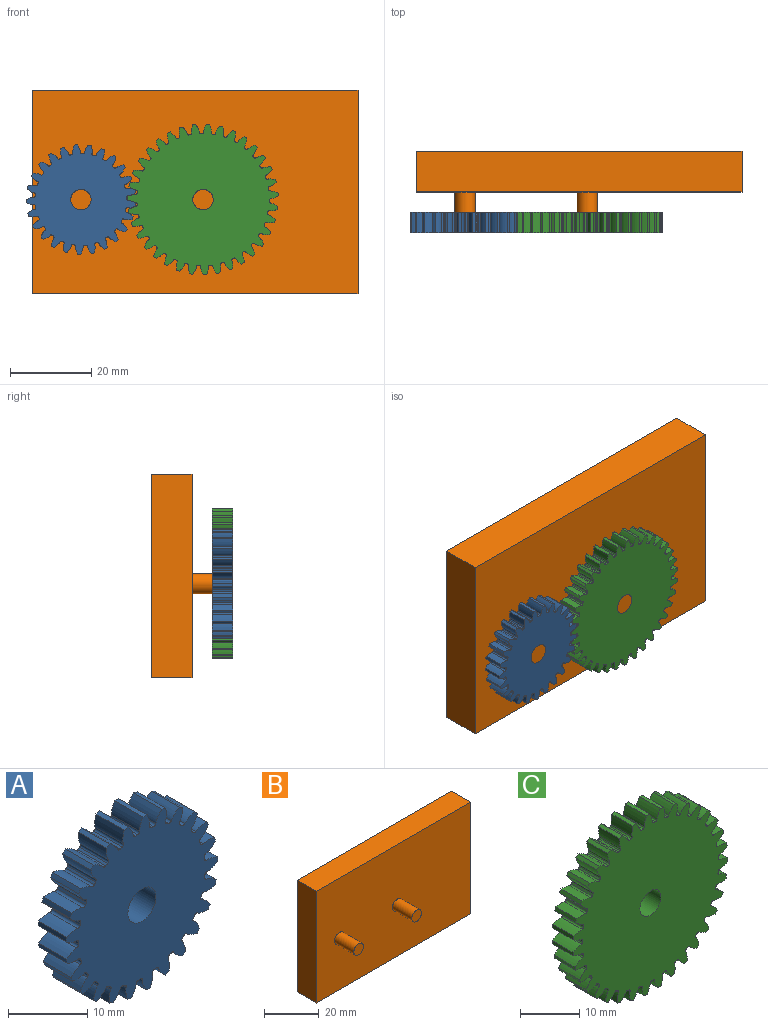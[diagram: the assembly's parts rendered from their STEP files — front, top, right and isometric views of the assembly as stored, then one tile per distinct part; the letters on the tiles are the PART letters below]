
ASSEMBLY  parts=3 mates=2
PART A: 153 faces, bbox 27x5x27 mm
  f0: extruded ~5x1.94mm, area 10.1mm2, adj f100,f101,f102,f103
  f1: cylinder r=11.25mm len=5mm, axis (0,1,0), area 1.9mm2, adj f101,f102,f103,f104
  f2: extruded ~5x1.71mm, area 10.1mm2, adj f3,f101,f102,f104
  f3: cylinder r=13.5mm len=5mm, axis (0,1,0), area 3.6mm2, adj f2,f4,f101,f102
  f4: extruded ~5x2mm, area 10.1mm2, adj f3,f101,f102,f105
  f5: cylinder r=11.25mm len=5mm, axis (0,1,0), area 1.9mm2, adj f101,f102,f105,f106
  f6: extruded ~5x1.44mm, area 10.1mm2, adj f7,f101,f102,f106
  f7: cylinder r=13.5mm len=5mm, axis (0,1,0), area 3.6mm2, adj f6,f8,f101,f102
  f8: extruded ~5x1.94mm, area 10.1mm2, adj f7,f101,f102,f107
  f9: cylinder r=11.25mm len=5mm, axis (0,1,0), area 1.9mm2, adj f101,f102,f107,f108
  f10: extruded ~5x1.74mm, area 10.1mm2, adj f11,f101,f102,f108
  f11: cylinder r=13.5mm len=5mm, axis (0,1,0), area 3.6mm2, adj f10,f12,f101,f102
  f12: extruded ~5x1.76mm, area 10.1mm2, adj f11,f101,f102,f109
  f13: cylinder r=11.25mm len=5mm, axis (0,1,0), area 1.9mm2, adj f101,f102,f109,f110
  f14: extruded ~5x1.93mm, area 10.1mm2, adj f15,f101,f102,f110
  f15: cylinder r=13.5mm len=5mm, axis (0,1,0), area 3.6mm2, adj f14,f16,f101,f102
  f16: extruded ~5x1.46mm, area 10.1mm2, adj f15,f101,f102,f111
  f17: cylinder r=11.25mm len=5mm, axis (0,1,0), area 1.9mm2, adj f101,f102,f111,f112
  f18: extruded ~5x2mm, area 10.1mm2, adj f19,f101,f102,f112
  f19: cylinder r=13.5mm len=5mm, axis (0,1,0), area 3.6mm2, adj f18,f20,f101,f102
  f20: extruded ~5x1.69mm, area 10.1mm2, adj f19,f101,f102,f113
  f21: cylinder r=11.25mm len=5mm, axis (0,1,0), area 1.9mm2, adj f101,f102,f113,f114
  f22: extruded ~5x1.95mm, area 10.1mm2, adj f23,f101,f102,f114
  f23: cylinder r=13.5mm len=5mm, axis (0,1,0), area 3.6mm2, adj f22,f24,f101,f102
  f24: extruded ~5x1.9mm, area 10.1mm2, adj f23,f101,f102,f115
  f25: cylinder r=11.25mm len=5mm, axis (0,1,0), area 1.9mm2, adj f101,f102,f115,f116
  f26: extruded ~5x1.77mm, area 10.1mm2, adj f27,f101,f102,f116
  f27: cylinder r=13.5mm len=5mm, axis (0,1,0), area 3.6mm2, adj f26,f28,f101,f102
  f28: extruded ~5x2mm, area 10.1mm2, adj f27,f101,f102,f117
  f29: cylinder r=11.25mm len=5mm, axis (0,1,0), area 1.9mm2, adj f101,f102,f117,f118
  f30: extruded ~5x1.48mm, area 10.1mm2, adj f31,f101,f102,f118
  f31: cylinder r=13.5mm len=5mm, axis (0,1,0), area 3.6mm2, adj f30,f32,f101,f102
  f32: extruded ~5x1.97mm, area 10.1mm2, adj f31,f101,f102,f119
  f33: cylinder r=11.25mm len=5mm, axis (0,1,0), area 1.9mm2, adj f101,f102,f119,f120
  f34: extruded ~5x1.67mm, area 10.1mm2, adj f35,f101,f102,f120
  f35: cylinder r=13.5mm len=5mm, axis (0,1,0), area 3.6mm2, adj f34,f36,f101,f102
  f36: extruded ~5x1.81mm, area 10.1mm2, adj f35,f101,f102,f121
  f37: cylinder r=11.25mm len=5mm, axis (0,1,0), area 1.9mm2, adj f101,f102,f121,f122
  f38: extruded ~5x1.89mm, area 10.1mm2, adj f39,f101,f102,f122
  f39: cylinder r=13.5mm len=5mm, axis (0,1,0), area 3.6mm2, adj f38,f40,f101,f102
  f40: extruded ~5x1.54mm, area 10.1mm2, adj f39,f101,f102,f123
  f41: cylinder r=11.25mm len=5mm, axis (0,1,0), area 1.9mm2, adj f101,f102,f123,f124
  f42: extruded ~5x2mm, area 10.1mm2, adj f43,f101,f102,f124
  f43: cylinder r=13.5mm len=5mm, axis (0,1,0), area 3.6mm2, adj f42,f44,f101,f102
  f44: extruded ~5x1.62mm, area 10.1mm2, adj f43,f101,f102,f125
  f45: cylinder r=11.25mm len=5mm, axis (0,1,0), area 1.9mm2, adj f101,f102,f125,f126
  f46: extruded ~5x1.97mm, area 10.1mm2, adj f47,f101,f102,f126
  f47: cylinder r=13.5mm len=5mm, axis (0,1,0), area 3.6mm2, adj f46,f48,f101,f102
  f48: extruded ~5x1.86mm, area 10.1mm2, adj f47,f101,f102,f127
  f49: cylinder r=11.25mm len=5mm, axis (0,1,0), area 1.9mm2, adj f101,f102,f127,f128
  f50: extruded ~5x1.83mm, area 10.1mm2, adj f51,f101,f102,f128
  f51: cylinder r=13.5mm len=5mm, axis (0,1,0), area 3.6mm2, adj f50,f52,f101,f102
  f52: extruded ~5x1.99mm, area 10.1mm2, adj f51,f101,f102,f129
  f53: cylinder r=11.25mm len=5mm, axis (0,1,0), area 1.9mm2, adj f101,f102,f129,f130
  f54: extruded ~5x1.56mm, area 10.1mm2, adj f55,f101,f102,f130
  f55: cylinder r=13.5mm len=5mm, axis (0,1,0), area 3.6mm2, adj f54,f56,f101,f102
  f56: extruded ~5x1.99mm, area 10.1mm2, adj f55,f101,f102,f131
  f57: cylinder r=11.25mm len=5mm, axis (0,1,0), area 1.9mm2, adj f101,f102,f131,f132
  f58: extruded ~5x1.6mm, area 10.1mm2, adj f59,f101,f102,f132
  f59: cylinder r=13.5mm len=5mm, axis (0,1,0), area 3.6mm2, adj f58,f60,f101,f102
  f60: extruded ~5x1.86mm, area 10.1mm2, adj f59,f101,f102,f133
  f61: cylinder r=11.25mm len=5mm, axis (0,1,0), area 1.9mm2, adj f101,f102,f133,f134
  f62: extruded ~5x1.85mm, area 10.1mm2, adj f63,f101,f102,f134
  f63: cylinder r=13.5mm len=5mm, axis (0,1,0), area 3.6mm2, adj f62,f64,f101,f102
  f64: extruded ~5x1.62mm, area 10.1mm2, adj f63,f101,f102,f135
  f65: cylinder r=11.25mm len=5mm, axis (0,1,0), area 1.9mm2, adj f101,f102,f135,f136
  f66: extruded ~5x1.98mm, area 10.1mm2, adj f67,f101,f102,f136
  f67: cylinder r=13.5mm len=5mm, axis (0,1,0), area 3.6mm2, adj f66,f68,f101,f102
  f68: extruded ~5x1.54mm, area 10.1mm2, adj f67,f101,f102,f137
  f69: cylinder r=11.25mm len=5mm, axis (0,1,0), area 1.9mm2, adj f101,f102,f137,f138
  f70: extruded ~5x1.99mm, area 10.1mm2, adj f71,f101,f102,f138
  f71: cylinder r=13.5mm len=5mm, axis (0,1,0), area 3.6mm2, adj f70,f72,f101,f102
  f72: extruded ~5x1.81mm, area 10.1mm2, adj f71,f101,f102,f139
  f73: cylinder r=11.25mm len=5mm, axis (0,1,0), area 1.9mm2, adj f101,f102,f139,f140
  f74: extruded ~5x1.87mm, area 10.1mm2, adj f75,f101,f102,f140
  f75: cylinder r=13.5mm len=5mm, axis (0,1,0), area 3.6mm2, adj f74,f76,f101,f102
  f76: extruded ~5x1.97mm, area 10.1mm2, adj f75,f101,f102,f141
  f77: cylinder r=11.25mm len=5mm, axis (0,1,0), area 1.9mm2, adj f101,f102,f141,f142
  f78: extruded ~5x1.64mm, area 10.1mm2, adj f79,f101,f102,f142
  f79: cylinder r=13.5mm len=5mm, axis (0,1,0), area 3.6mm2, adj f78,f80,f101,f102
  f80: extruded ~5x2mm, area 10.1mm2, adj f79,f101,f102,f143
  f81: cylinder r=11.25mm len=5mm, axis (0,1,0), area 1.9mm2, adj f101,f102,f143,f144
  f82: extruded ~5x1.52mm, area 10.1mm2, adj f83,f101,f102,f144
  f83: cylinder r=13.5mm len=5mm, axis (0,1,0), area 3.6mm2, adj f82,f84,f101,f102
  f84: extruded ~5x1.9mm, area 10.1mm2, adj f83,f101,f102,f145
  f85: cylinder r=11.25mm len=5mm, axis (0,1,0), area 1.9mm2, adj f101,f102,f145,f146
  f86: extruded ~5x1.8mm, area 10.1mm2, adj f87,f101,f102,f146
  f87: cylinder r=13.5mm len=5mm, axis (0,1,0), area 3.6mm2, adj f86,f88,f101,f102
  f88: extruded ~5x1.69mm, area 10.1mm2, adj f87,f101,f102,f147
  f89: cylinder r=11.25mm len=5mm, axis (0,1,0), area 1.9mm2, adj f101,f102,f147,f148
  f90: extruded ~5x1.96mm, area 10.1mm2, adj f91,f101,f102,f148
  f91: cylinder r=13.5mm len=5mm, axis (0,1,0), area 3.6mm2, adj f90,f92,f101,f102
  f92: extruded ~5x1.46mm, area 10.1mm2, adj f91,f101,f102,f149
  f93: cylinder r=11.25mm len=5mm, axis (0,1,0), area 1.9mm2, adj f101,f102,f149,f150
  f94: extruded ~5x2mm, area 10.1mm2, adj f95,f101,f102,f150
  f95: cylinder r=13.5mm len=5mm, axis (0,1,0), area 3.6mm2, adj f94,f96,f101,f102
  f96: extruded ~5x1.75mm, area 10.1mm2, adj f95,f101,f102,f151
  f97: cylinder r=11.25mm len=5mm, axis (0,1,0), area 1.9mm2, adj f101,f102,f151,f152
  f98: extruded ~5x1.91mm, area 10.1mm2, adj f100,f101,f102,f152
  f99: cylinder r=2.5mm len=5mm, axis (0,1,0), area 78.5mm2, adj f101,f102
  f100: cylinder r=13.5mm len=5mm, axis (0,1,0), area 3.6mm2, adj f0,f98,f101,f102
  f101: plane 26.98x26.97mm, normal (0,-1,0), area 463.9mm2, adj f0,f1,f2,f3,f4,f5,f6,f7
  f102: plane 26.98x26.97mm, normal (0,1,0), area 463.9mm2, adj f0,f1,f2,f3,f4,f5,f6,f7
  f103: cylinder r=0.36mm len=5mm, axis (0,1,0), area 2.8mm2, adj f0,f1,f101,f102
  f104: cylinder r=0.36mm len=5mm, axis (0,1,0), area 2.8mm2, adj f1,f2,f101,f102
  f105: cylinder r=0.36mm len=5mm, axis (0,1,0), area 2.8mm2, adj f4,f5,f101,f102
  f106: cylinder r=0.36mm len=5mm, axis (0,1,0), area 2.8mm2, adj f5,f6,f101,f102
  f107: cylinder r=0.36mm len=5mm, axis (0,1,0), area 2.8mm2, adj f8,f9,f101,f102
  f108: cylinder r=0.36mm len=5mm, axis (0,1,0), area 2.8mm2, adj f9,f10,f101,f102
  f109: cylinder r=0.36mm len=5mm, axis (0,1,0), area 2.8mm2, adj f12,f13,f101,f102
  f110: cylinder r=0.36mm len=5mm, axis (0,1,0), area 2.8mm2, adj f13,f14,f101,f102
  f111: cylinder r=0.36mm len=5mm, axis (0,1,0), area 2.8mm2, adj f16,f17,f101,f102
  f112: cylinder r=0.36mm len=5mm, axis (0,1,0), area 2.8mm2, adj f17,f18,f101,f102
  f113: cylinder r=0.36mm len=5mm, axis (0,1,0), area 2.8mm2, adj f20,f21,f101,f102
  f114: cylinder r=0.36mm len=5mm, axis (0,1,0), area 2.8mm2, adj f21,f22,f101,f102
  f115: cylinder r=0.36mm len=5mm, axis (0,1,0), area 2.8mm2, adj f24,f25,f101,f102
  f116: cylinder r=0.36mm len=5mm, axis (0,1,0), area 2.8mm2, adj f25,f26,f101,f102
  f117: cylinder r=0.36mm len=5mm, axis (0,1,0), area 2.8mm2, adj f28,f29,f101,f102
  f118: cylinder r=0.36mm len=5mm, axis (0,1,0), area 2.8mm2, adj f29,f30,f101,f102
  f119: cylinder r=0.36mm len=5mm, axis (0,1,0), area 2.8mm2, adj f32,f33,f101,f102
  f120: cylinder r=0.36mm len=5mm, axis (0,1,0), area 2.8mm2, adj f33,f34,f101,f102
  f121: cylinder r=0.36mm len=5mm, axis (0,1,0), area 2.8mm2, adj f36,f37,f101,f102
  f122: cylinder r=0.36mm len=5mm, axis (0,1,0), area 2.8mm2, adj f37,f38,f101,f102
  f123: cylinder r=0.36mm len=5mm, axis (0,1,0), area 2.8mm2, adj f40,f41,f101,f102
  f124: cylinder r=0.36mm len=5mm, axis (0,1,0), area 2.8mm2, adj f41,f42,f101,f102
  f125: cylinder r=0.36mm len=5mm, axis (0,1,0), area 2.8mm2, adj f44,f45,f101,f102
  f126: cylinder r=0.36mm len=5mm, axis (0,1,0), area 2.8mm2, adj f45,f46,f101,f102
  f127: cylinder r=0.36mm len=5mm, axis (0,1,0), area 2.8mm2, adj f48,f49,f101,f102
  f128: cylinder r=0.36mm len=5mm, axis (0,1,0), area 2.8mm2, adj f49,f50,f101,f102
  f129: cylinder r=0.36mm len=5mm, axis (0,1,0), area 2.8mm2, adj f52,f53,f101,f102
  f130: cylinder r=0.36mm len=5mm, axis (0,1,0), area 2.8mm2, adj f53,f54,f101,f102
  f131: cylinder r=0.36mm len=5mm, axis (0,1,0), area 2.8mm2, adj f56,f57,f101,f102
  f132: cylinder r=0.36mm len=5mm, axis (0,1,0), area 2.8mm2, adj f57,f58,f101,f102
  f133: cylinder r=0.36mm len=5mm, axis (0,1,0), area 2.8mm2, adj f60,f61,f101,f102
  f134: cylinder r=0.36mm len=5mm, axis (0,1,0), area 2.8mm2, adj f61,f62,f101,f102
  f135: cylinder r=0.36mm len=5mm, axis (0,1,0), area 2.8mm2, adj f64,f65,f101,f102
  f136: cylinder r=0.36mm len=5mm, axis (0,1,0), area 2.8mm2, adj f65,f66,f101,f102
  f137: cylinder r=0.36mm len=5mm, axis (0,1,0), area 2.8mm2, adj f68,f69,f101,f102
  f138: cylinder r=0.36mm len=5mm, axis (0,1,0), area 2.8mm2, adj f69,f70,f101,f102
  f139: cylinder r=0.36mm len=5mm, axis (0,1,0), area 2.8mm2, adj f72,f73,f101,f102
  f140: cylinder r=0.36mm len=5mm, axis (0,1,0), area 2.8mm2, adj f73,f74,f101,f102
  f141: cylinder r=0.36mm len=5mm, axis (0,1,0), area 2.8mm2, adj f76,f77,f101,f102
  f142: cylinder r=0.36mm len=5mm, axis (0,1,0), area 2.8mm2, adj f77,f78,f101,f102
  f143: cylinder r=0.36mm len=5mm, axis (0,1,0), area 2.8mm2, adj f80,f81,f101,f102
  f144: cylinder r=0.36mm len=5mm, axis (0,1,0), area 2.8mm2, adj f81,f82,f101,f102
  f145: cylinder r=0.36mm len=5mm, axis (0,1,0), area 2.8mm2, adj f84,f85,f101,f102
  f146: cylinder r=0.36mm len=5mm, axis (0,1,0), area 2.8mm2, adj f85,f86,f101,f102
  f147: cylinder r=0.36mm len=5mm, axis (0,1,0), area 2.8mm2, adj f88,f89,f101,f102
  f148: cylinder r=0.36mm len=5mm, axis (0,1,0), area 2.8mm2, adj f89,f90,f101,f102
  f149: cylinder r=0.36mm len=5mm, axis (0,1,0), area 2.8mm2, adj f92,f93,f101,f102
  f150: cylinder r=0.36mm len=5mm, axis (0,1,0), area 2.8mm2, adj f93,f94,f101,f102
  f151: cylinder r=0.36mm len=5mm, axis (0,1,0), area 2.8mm2, adj f96,f97,f101,f102
  f152: cylinder r=0.36mm len=5mm, axis (0,1,0), area 2.8mm2, adj f97,f98,f101,f102
PART B: 10 faces, bbox 80x20x50 mm
  f0: plane 50x10mm, normal (-1,0,0), area 500mm2, adj f1,f3,f4,f5
  f1: plane 80x10mm, normal (0,0,-1), area 800mm2, adj f0,f2,f4,f5
  f2: plane 50x10mm, normal (1,0,0), area 500mm2, adj f1,f3,f4,f5
  f3: plane 80x10mm, normal (0,0,1), area 800mm2, adj f0,f2,f4,f5
  f4: plane 80x50mm, normal (0,-1,0), area 3960.7mm2, adj f0,f1,f2,f3,f6,f8
  f5: plane 80x50mm, normal (0,1,0), area 4000mm2, adj f0,f1,f2,f3
  f6: cylinder r=2.5mm len=10mm, axis (0,1,0), area 157.1mm2, adj f4,f7
  f7: plane 5x5mm, normal (0,-1,0), area 19.6mm2, adj f6
  f8: cylinder r=2.5mm len=10mm, axis (0,1,0), area 157.1mm2, adj f4,f9
  f9: plane 5x5mm, normal (0,-1,0), area 19.6mm2, adj f8
PART C: 213 faces, bbox 37x5x37 mm
  f0: extruded ~5x1.98mm, area 10.5mm2, adj f140,f141,f142,f143
  f1: cylinder r=16.25mm len=5mm, axis (0,1,0), area 1.8mm2, adj f141,f142,f143,f144
  f2: extruded ~5x1.86mm, area 10.5mm2, adj f3,f141,f142,f144
  f3: cylinder r=18.5mm len=5mm, axis (0,1,0), area 3.7mm2, adj f2,f4,f141,f142
  f4: extruded ~5x2.06mm, area 10.5mm2, adj f3,f141,f142,f145
  f5: cylinder r=16.25mm len=5mm, axis (0,1,0), area 1.8mm2, adj f141,f142,f145,f146
  f6: extruded ~5x1.67mm, area 10.5mm2, adj f7,f141,f142,f146
  f7: cylinder r=18.5mm len=5mm, axis (0,1,0), area 3.7mm2, adj f6,f8,f141,f142
  f8: extruded ~5x2.08mm, area 10.5mm2, adj f7,f141,f142,f147
  f9: cylinder r=16.25mm len=5mm, axis (0,1,0), area 1.8mm2, adj f141,f142,f147,f148
  f10: extruded ~5x1.52mm, area 10.5mm2, adj f11,f141,f142,f148
  f11: cylinder r=18.5mm len=5mm, axis (0,1,0), area 3.7mm2, adj f10,f12,f141,f142
  f12: extruded ~5x2.03mm, area 10.5mm2, adj f11,f141,f142,f149
  f13: cylinder r=16.25mm len=5mm, axis (0,1,0), area 1.8mm2, adj f141,f142,f149,f150
  f14: extruded ~5x1.75mm, area 10.5mm2, adj f15,f141,f142,f150
  f15: cylinder r=18.5mm len=5mm, axis (0,1,0), area 3.7mm2, adj f14,f16,f141,f142
  f16: extruded ~5x1.91mm, area 10.5mm2, adj f15,f141,f142,f151
  f17: cylinder r=16.25mm len=5mm, axis (0,1,0), area 1.8mm2, adj f141,f142,f151,f152
  f18: extruded ~5x1.92mm, area 10.5mm2, adj f19,f141,f142,f152
  f19: cylinder r=18.5mm len=5mm, axis (0,1,0), area 3.7mm2, adj f18,f20,f141,f142
  f20: extruded ~5x1.73mm, area 10.5mm2, adj f19,f141,f142,f153
  f21: cylinder r=16.25mm len=5mm, axis (0,1,0), area 1.8mm2, adj f141,f142,f153,f154
  f22: extruded ~5x2.03mm, area 10.5mm2, adj f23,f141,f142,f154
  f23: cylinder r=18.5mm len=5mm, axis (0,1,0), area 3.7mm2, adj f22,f24,f141,f142
  f24: extruded ~5x1.5mm, area 10.5mm2, adj f23,f141,f142,f155
  f25: cylinder r=16.25mm len=5mm, axis (0,1,0), area 1.8mm2, adj f141,f142,f155,f156
  f26: extruded ~5x2.08mm, area 10.5mm2, adj f27,f141,f142,f156
  f27: cylinder r=18.5mm len=5mm, axis (0,1,0), area 3.7mm2, adj f26,f28,f141,f142
  f28: extruded ~5x1.69mm, area 10.5mm2, adj f27,f141,f142,f157
  f29: cylinder r=16.25mm len=5mm, axis (0,1,0), area 1.8mm2, adj f141,f142,f157,f158
  f30: extruded ~5x2.06mm, area 10.5mm2, adj f31,f141,f142,f158
  f31: cylinder r=18.5mm len=5mm, axis (0,1,0), area 3.7mm2, adj f30,f32,f141,f142
  f32: extruded ~5x1.88mm, area 10.5mm2, adj f31,f141,f142,f159
  f33: cylinder r=16.25mm len=5mm, axis (0,1,0), area 1.8mm2, adj f141,f142,f159,f160
  f34: extruded ~5x1.97mm, area 10.5mm2, adj f35,f141,f142,f160
  f35: cylinder r=18.5mm len=5mm, axis (0,1,0), area 3.7mm2, adj f34,f36,f141,f142
  f36: extruded ~5x2.01mm, area 10.5mm2, adj f35,f141,f142,f161
  f37: cylinder r=16.25mm len=5mm, axis (0,1,0), area 1.8mm2, adj f141,f142,f161,f162
  f38: extruded ~5x1.82mm, area 10.5mm2, adj f39,f141,f142,f162
  f39: cylinder r=18.5mm len=5mm, axis (0,1,0), area 3.7mm2, adj f38,f40,f141,f142
  f40: extruded ~5x2.07mm, area 10.5mm2, adj f39,f141,f142,f163
  f41: cylinder r=16.25mm len=5mm, axis (0,1,0), area 1.8mm2, adj f141,f142,f163,f164
  f42: extruded ~5x1.61mm, area 10.5mm2, adj f43,f141,f142,f164
  f43: cylinder r=18.5mm len=5mm, axis (0,1,0), area 3.7mm2, adj f42,f44,f141,f142
  f44: extruded ~5x2.07mm, area 10.5mm2, adj f43,f141,f142,f165
  f45: cylinder r=16.25mm len=5mm, axis (0,1,0), area 1.8mm2, adj f141,f142,f165,f166
  f46: extruded ~5x1.58mm, area 10.5mm2, adj f47,f141,f142,f166
  f47: cylinder r=18.5mm len=5mm, axis (0,1,0), area 3.7mm2, adj f46,f48,f141,f142
  f48: extruded ~5x2mm, area 10.5mm2, adj f47,f141,f142,f167
  f49: cylinder r=16.25mm len=5mm, axis (0,1,0), area 1.8mm2, adj f141,f142,f167,f168
  f50: extruded ~5x1.8mm, area 10.5mm2, adj f51,f141,f142,f168
  f51: cylinder r=18.5mm len=5mm, axis (0,1,0), area 3.7mm2, adj f50,f52,f141,f142
  f52: extruded ~5x1.87mm, area 10.5mm2, adj f51,f141,f142,f169
  f53: cylinder r=16.25mm len=5mm, axis (0,1,0), area 1.8mm2, adj f141,f142,f169,f170
  f54: extruded ~5x1.96mm, area 10.5mm2, adj f55,f141,f142,f170
  f55: cylinder r=18.5mm len=5mm, axis (0,1,0), area 3.7mm2, adj f54,f56,f141,f142
  f56: extruded ~5x1.68mm, area 10.5mm2, adj f55,f141,f142,f171
  f57: cylinder r=16.25mm len=5mm, axis (0,1,0), area 1.8mm2, adj f141,f142,f171,f172
  f58: extruded ~5x2.05mm, area 10.5mm2, adj f59,f141,f142,f172
  f59: cylinder r=18.5mm len=5mm, axis (0,1,0), area 3.7mm2, adj f58,f60,f141,f142
  f60: extruded ~5x1.51mm, area 10.5mm2, adj f59,f141,f142,f173
  f61: cylinder r=16.25mm len=5mm, axis (0,1,0), area 1.8mm2, adj f141,f142,f173,f174
  f62: extruded ~5x2.08mm, area 10.5mm2, adj f63,f141,f142,f174
  f63: cylinder r=18.5mm len=5mm, axis (0,1,0), area 3.7mm2, adj f62,f64,f141,f142
  f64: extruded ~5x1.74mm, area 10.5mm2, adj f63,f141,f142,f175
  f65: cylinder r=16.25mm len=5mm, axis (0,1,0), area 1.8mm2, adj f141,f142,f175,f176
  f66: extruded ~5x2.04mm, area 10.5mm2, adj f67,f141,f142,f176
  f67: cylinder r=18.5mm len=5mm, axis (0,1,0), area 3.7mm2, adj f66,f68,f141,f142
  f68: extruded ~5x1.92mm, area 10.5mm2, adj f67,f141,f142,f177
  f69: cylinder r=16.25mm len=5mm, axis (0,1,0), area 1.8mm2, adj f141,f142,f177,f178
  f70: extruded ~5x1.94mm, area 10.5mm2, adj f71,f141,f142,f178
  f71: cylinder r=18.5mm len=5mm, axis (0,1,0), area 3.7mm2, adj f70,f72,f141,f142
  f72: extruded ~5x2.03mm, area 10.5mm2, adj f71,f141,f142,f179
  f73: cylinder r=16.25mm len=5mm, axis (0,1,0), area 1.8mm2, adj f141,f142,f179,f180
  f74: extruded ~5x1.77mm, area 10.5mm2, adj f75,f141,f142,f180
  f75: cylinder r=18.5mm len=5mm, axis (0,1,0), area 3.7mm2, adj f74,f76,f141,f142
  f76: extruded ~5x2.08mm, area 10.5mm2, adj f75,f141,f142,f181
  f77: cylinder r=16.25mm len=5mm, axis (0,1,0), area 1.8mm2, adj f141,f142,f181,f182
  f78: extruded ~5x1.55mm, area 10.5mm2, adj f79,f141,f142,f182
  f79: cylinder r=18.5mm len=5mm, axis (0,1,0), area 3.7mm2, adj f78,f80,f141,f142
  f80: extruded ~5x2.06mm, area 10.5mm2, adj f79,f141,f142,f183
  f81: cylinder r=16.25mm len=5mm, axis (0,1,0), area 1.8mm2, adj f141,f142,f183,f184
  f82: extruded ~5x1.64mm, area 10.5mm2, adj f83,f141,f142,f184
  f83: cylinder r=18.5mm len=5mm, axis (0,1,0), area 3.7mm2, adj f82,f84,f141,f142
  f84: extruded ~5x1.98mm, area 10.5mm2, adj f83,f141,f142,f185
  f85: cylinder r=16.25mm len=5mm, axis (0,1,0), area 1.8mm2, adj f141,f142,f185,f186
  f86: extruded ~5x1.84mm, area 10.5mm2, adj f87,f141,f142,f186
  f87: cylinder r=18.5mm len=5mm, axis (0,1,0), area 3.7mm2, adj f86,f88,f141,f142
  f88: extruded ~5x1.83mm, area 10.5mm2, adj f87,f141,f142,f187
  f89: cylinder r=16.25mm len=5mm, axis (0,1,0), area 1.8mm2, adj f141,f142,f187,f188
  f90: extruded ~5x1.99mm, area 10.5mm2, adj f91,f141,f142,f188
  f91: cylinder r=18.5mm len=5mm, axis (0,1,0), area 3.7mm2, adj f90,f92,f141,f142
  f92: extruded ~5x1.62mm, area 10.5mm2, adj f91,f141,f142,f189
  f93: cylinder r=16.25mm len=5mm, axis (0,1,0), area 1.8mm2, adj f141,f142,f189,f190
  f94: extruded ~5x2.07mm, area 10.5mm2, adj f95,f141,f142,f190
  f95: cylinder r=18.5mm len=5mm, axis (0,1,0), area 3.7mm2, adj f94,f96,f141,f142
  f96: extruded ~5x1.57mm, area 10.5mm2, adj f95,f141,f142,f191
  f97: cylinder r=16.25mm len=5mm, axis (0,1,0), area 1.8mm2, adj f141,f142,f191,f192
  f98: extruded ~5x2.08mm, area 10.5mm2, adj f99,f141,f142,f192
  f99: cylinder r=18.5mm len=5mm, axis (0,1,0), area 3.7mm2, adj f98,f100,f141,f142
  f100: extruded ~5x1.79mm, area 10.5mm2, adj f99,f141,f142,f193
  f101: cylinder r=16.25mm len=5mm, axis (0,1,0), area 1.8mm2, adj f141,f142,f193,f194
  f102: extruded ~5x2.02mm, area 10.5mm2, adj f103,f141,f142,f194
  f103: cylinder r=18.5mm len=5mm, axis (0,1,0), area 3.7mm2, adj f102,f104,f141,f142
  f104: extruded ~5x1.95mm, area 10.5mm2, adj f103,f141,f142,f195
  f105: cylinder r=16.25mm len=5mm, axis (0,1,0), area 1.8mm2, adj f141,f142,f195,f196
  f106: extruded ~5x1.9mm, area 10.5mm2, adj f107,f141,f142,f196
  f107: cylinder r=18.5mm len=5mm, axis (0,1,0), area 3.7mm2, adj f106,f108,f141,f142
  f108: extruded ~5x2.05mm, area 10.5mm2, adj f107,f141,f142,f197
  f109: cylinder r=16.25mm len=5mm, axis (0,1,0), area 1.8mm2, adj f141,f142,f197,f198
  f110: extruded ~5x1.72mm, area 10.5mm2, adj f111,f141,f142,f198
  f111: cylinder r=18.5mm len=5mm, axis (0,1,0), area 3.7mm2, adj f110,f112,f141,f142
  f112: extruded ~5x2.08mm, area 10.5mm2, adj f111,f141,f142,f199
  f113: cylinder r=16.25mm len=5mm, axis (0,1,0), area 1.8mm2, adj f141,f142,f199,f200
  f114: extruded ~5x1.49mm, area 10.5mm2, adj f115,f141,f142,f200
  f115: cylinder r=18.5mm len=5mm, axis (0,1,0), area 3.7mm2, adj f114,f116,f141,f142
  f116: extruded ~5x2.05mm, area 10.5mm2, adj f115,f141,f142,f201
  f117: cylinder r=16.25mm len=5mm, axis (0,1,0), area 1.8mm2, adj f141,f142,f201,f202
  f118: extruded ~5x1.7mm, area 10.5mm2, adj f119,f141,f142,f202
  f119: cylinder r=18.5mm len=5mm, axis (0,1,0), area 3.7mm2, adj f118,f120,f141,f142
  f120: extruded ~5x1.95mm, area 10.5mm2, adj f119,f141,f142,f203
  f121: cylinder r=16.25mm len=5mm, axis (0,1,0), area 1.8mm2, adj f141,f142,f203,f204
  f122: extruded ~5x1.88mm, area 10.5mm2, adj f123,f141,f142,f204
  f123: cylinder r=18.5mm len=5mm, axis (0,1,0), area 3.7mm2, adj f122,f124,f141,f142
  f124: extruded ~5x1.78mm, area 10.5mm2, adj f123,f141,f142,f205
  f125: cylinder r=16.25mm len=5mm, axis (0,1,0), area 1.8mm2, adj f141,f142,f205,f206
  f126: extruded ~5x2.01mm, area 10.5mm2, adj f127,f141,f142,f206
  f127: cylinder r=18.5mm len=5mm, axis (0,1,0), area 3.7mm2, adj f126,f128,f141,f142
  f128: extruded ~5x1.56mm, area 10.5mm2, adj f127,f141,f142,f207
  f129: cylinder r=16.25mm len=5mm, axis (0,1,0), area 1.8mm2, adj f141,f142,f207,f208
  f130: extruded ~5x2.07mm, area 10.5mm2, adj f131,f141,f142,f208
  f131: cylinder r=18.5mm len=5mm, axis (0,1,0), area 3.7mm2, adj f130,f132,f141,f142
  f132: extruded ~5x1.63mm, area 10.5mm2, adj f131,f141,f142,f209
  f133: cylinder r=16.25mm len=5mm, axis (0,1,0), area 1.8mm2, adj f141,f142,f209,f210
  f134: extruded ~5x2.07mm, area 10.5mm2, adj f135,f141,f142,f210
  f135: cylinder r=18.5mm len=5mm, axis (0,1,0), area 3.7mm2, adj f134,f136,f141,f142
  f136: extruded ~5x1.84mm, area 10.5mm2, adj f135,f141,f142,f211
  f137: cylinder r=16.25mm len=5mm, axis (0,1,0), area 1.8mm2, adj f141,f142,f211,f212
  f138: extruded ~5x2mm, area 10.5mm2, adj f140,f141,f142,f212
  f139: cylinder r=2.5mm len=5mm, axis (0,1,0), area 78.5mm2, adj f141,f142
  f140: cylinder r=18.5mm len=5mm, axis (0,1,0), area 3.7mm2, adj f0,f138,f141,f142
  f141: plane 36.99x36.97mm, normal (0,-1,0), area 933.6mm2, adj f0,f1,f2,f3,f4,f5,f6,f7
  f142: plane 36.99x36.97mm, normal (0,1,0), area 933.6mm2, adj f0,f1,f2,f3,f4,f5,f6,f7
  f143: cylinder r=0.32mm len=5mm, axis (0,1,0), area 2.3mm2, adj f0,f1,f141,f142
  f144: cylinder r=0.32mm len=5mm, axis (0,1,0), area 2.3mm2, adj f1,f2,f141,f142
  f145: cylinder r=0.32mm len=5mm, axis (0,1,0), area 2.3mm2, adj f4,f5,f141,f142
  f146: cylinder r=0.32mm len=5mm, axis (0,1,0), area 2.3mm2, adj f5,f6,f141,f142
  f147: cylinder r=0.32mm len=5mm, axis (0,1,0), area 2.3mm2, adj f8,f9,f141,f142
  f148: cylinder r=0.32mm len=5mm, axis (0,1,0), area 2.3mm2, adj f9,f10,f141,f142
  f149: cylinder r=0.32mm len=5mm, axis (0,1,0), area 2.3mm2, adj f12,f13,f141,f142
  f150: cylinder r=0.32mm len=5mm, axis (0,1,0), area 2.3mm2, adj f13,f14,f141,f142
  f151: cylinder r=0.32mm len=5mm, axis (0,1,0), area 2.3mm2, adj f16,f17,f141,f142
  f152: cylinder r=0.32mm len=5mm, axis (0,1,0), area 2.3mm2, adj f17,f18,f141,f142
  f153: cylinder r=0.32mm len=5mm, axis (0,1,0), area 2.3mm2, adj f20,f21,f141,f142
  f154: cylinder r=0.32mm len=5mm, axis (0,1,0), area 2.3mm2, adj f21,f22,f141,f142
  f155: cylinder r=0.32mm len=5mm, axis (0,1,0), area 2.3mm2, adj f24,f25,f141,f142
  f156: cylinder r=0.32mm len=5mm, axis (0,1,0), area 2.3mm2, adj f25,f26,f141,f142
  f157: cylinder r=0.32mm len=5mm, axis (0,1,0), area 2.3mm2, adj f28,f29,f141,f142
  f158: cylinder r=0.32mm len=5mm, axis (0,1,0), area 2.3mm2, adj f29,f30,f141,f142
  f159: cylinder r=0.32mm len=5mm, axis (0,1,0), area 2.3mm2, adj f32,f33,f141,f142
  f160: cylinder r=0.32mm len=5mm, axis (0,1,0), area 2.3mm2, adj f33,f34,f141,f142
  f161: cylinder r=0.32mm len=5mm, axis (0,1,0), area 2.3mm2, adj f36,f37,f141,f142
  f162: cylinder r=0.32mm len=5mm, axis (0,1,0), area 2.3mm2, adj f37,f38,f141,f142
  f163: cylinder r=0.32mm len=5mm, axis (0,1,0), area 2.3mm2, adj f40,f41,f141,f142
  f164: cylinder r=0.32mm len=5mm, axis (0,1,0), area 2.3mm2, adj f41,f42,f141,f142
  f165: cylinder r=0.32mm len=5mm, axis (0,1,0), area 2.3mm2, adj f44,f45,f141,f142
  f166: cylinder r=0.32mm len=5mm, axis (0,1,0), area 2.3mm2, adj f45,f46,f141,f142
  f167: cylinder r=0.32mm len=5mm, axis (0,1,0), area 2.3mm2, adj f48,f49,f141,f142
  f168: cylinder r=0.32mm len=5mm, axis (0,1,0), area 2.3mm2, adj f49,f50,f141,f142
  f169: cylinder r=0.32mm len=5mm, axis (0,1,0), area 2.3mm2, adj f52,f53,f141,f142
  f170: cylinder r=0.32mm len=5mm, axis (0,1,0), area 2.3mm2, adj f53,f54,f141,f142
  f171: cylinder r=0.32mm len=5mm, axis (0,1,0), area 2.3mm2, adj f56,f57,f141,f142
  f172: cylinder r=0.32mm len=5mm, axis (0,1,0), area 2.3mm2, adj f57,f58,f141,f142
  f173: cylinder r=0.32mm len=5mm, axis (0,1,0), area 2.3mm2, adj f60,f61,f141,f142
  f174: cylinder r=0.32mm len=5mm, axis (0,1,0), area 2.3mm2, adj f61,f62,f141,f142
  f175: cylinder r=0.32mm len=5mm, axis (0,1,0), area 2.3mm2, adj f64,f65,f141,f142
  f176: cylinder r=0.32mm len=5mm, axis (0,1,0), area 2.3mm2, adj f65,f66,f141,f142
  f177: cylinder r=0.32mm len=5mm, axis (0,1,0), area 2.3mm2, adj f68,f69,f141,f142
  f178: cylinder r=0.32mm len=5mm, axis (0,1,0), area 2.3mm2, adj f69,f70,f141,f142
  f179: cylinder r=0.32mm len=5mm, axis (0,1,0), area 2.3mm2, adj f72,f73,f141,f142
  f180: cylinder r=0.32mm len=5mm, axis (0,1,0), area 2.3mm2, adj f73,f74,f141,f142
  f181: cylinder r=0.32mm len=5mm, axis (0,1,0), area 2.3mm2, adj f76,f77,f141,f142
  f182: cylinder r=0.32mm len=5mm, axis (0,1,0), area 2.3mm2, adj f77,f78,f141,f142
  f183: cylinder r=0.32mm len=5mm, axis (0,1,0), area 2.3mm2, adj f80,f81,f141,f142
  f184: cylinder r=0.32mm len=5mm, axis (0,1,0), area 2.3mm2, adj f81,f82,f141,f142
  f185: cylinder r=0.32mm len=5mm, axis (0,1,0), area 2.3mm2, adj f84,f85,f141,f142
  f186: cylinder r=0.32mm len=5mm, axis (0,1,0), area 2.3mm2, adj f85,f86,f141,f142
  f187: cylinder r=0.32mm len=5mm, axis (0,1,0), area 2.3mm2, adj f88,f89,f141,f142
  f188: cylinder r=0.32mm len=5mm, axis (0,1,0), area 2.3mm2, adj f89,f90,f141,f142
  f189: cylinder r=0.32mm len=5mm, axis (0,1,0), area 2.3mm2, adj f92,f93,f141,f142
  f190: cylinder r=0.32mm len=5mm, axis (0,1,0), area 2.3mm2, adj f93,f94,f141,f142
  f191: cylinder r=0.32mm len=5mm, axis (0,1,0), area 2.3mm2, adj f96,f97,f141,f142
  f192: cylinder r=0.32mm len=5mm, axis (0,1,0), area 2.3mm2, adj f97,f98,f141,f142
  f193: cylinder r=0.32mm len=5mm, axis (0,1,0), area 2.3mm2, adj f100,f101,f141,f142
  f194: cylinder r=0.32mm len=5mm, axis (0,1,0), area 2.3mm2, adj f101,f102,f141,f142
  f195: cylinder r=0.32mm len=5mm, axis (0,1,0), area 2.3mm2, adj f104,f105,f141,f142
  f196: cylinder r=0.32mm len=5mm, axis (0,1,0), area 2.3mm2, adj f105,f106,f141,f142
  f197: cylinder r=0.32mm len=5mm, axis (0,1,0), area 2.3mm2, adj f108,f109,f141,f142
  f198: cylinder r=0.32mm len=5mm, axis (0,1,0), area 2.3mm2, adj f109,f110,f141,f142
  f199: cylinder r=0.32mm len=5mm, axis (0,1,0), area 2.3mm2, adj f112,f113,f141,f142
  f200: cylinder r=0.32mm len=5mm, axis (0,1,0), area 2.3mm2, adj f113,f114,f141,f142
  f201: cylinder r=0.32mm len=5mm, axis (0,1,0), area 2.3mm2, adj f116,f117,f141,f142
  f202: cylinder r=0.32mm len=5mm, axis (0,1,0), area 2.3mm2, adj f117,f118,f141,f142
  f203: cylinder r=0.32mm len=5mm, axis (0,1,0), area 2.3mm2, adj f120,f121,f141,f142
  f204: cylinder r=0.32mm len=5mm, axis (0,1,0), area 2.3mm2, adj f121,f122,f141,f142
  f205: cylinder r=0.32mm len=5mm, axis (0,1,0), area 2.3mm2, adj f124,f125,f141,f142
  f206: cylinder r=0.32mm len=5mm, axis (0,1,0), area 2.3mm2, adj f125,f126,f141,f142
  f207: cylinder r=0.32mm len=5mm, axis (0,1,0), area 2.3mm2, adj f128,f129,f141,f142
  f208: cylinder r=0.32mm len=5mm, axis (0,1,0), area 2.3mm2, adj f129,f130,f141,f142
  f209: cylinder r=0.32mm len=5mm, axis (0,1,0), area 2.3mm2, adj f132,f133,f141,f142
  f210: cylinder r=0.32mm len=5mm, axis (0,1,0), area 2.3mm2, adj f133,f134,f141,f142
  f211: cylinder r=0.32mm len=5mm, axis (0,1,0), area 2.3mm2, adj f136,f137,f141,f142
  f212: cylinder r=0.32mm len=5mm, axis (0,1,0), area 2.3mm2, adj f137,f138,f141,f142
PLACE A rot(axis=(0,1,0),136.4deg) t=(-19.83,-7.68,-13.06)mm
PLACE B t=(-9.83,7.32,-13.06)mm fixed
PLACE C rot(axis=(0,-1,0),97.4deg) t=(10.17,-7.68,-13.06)mm
MATE revolute B.f6 <-> A.f3  axis (0,-1,0) through (-19.83,-12.68,-13.06)mm
MATE revolute C.f3 <-> B.f8  axis (0,-1,0) through (10.17,-12.68,-13.06)mm
